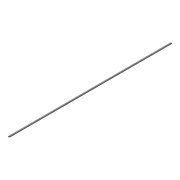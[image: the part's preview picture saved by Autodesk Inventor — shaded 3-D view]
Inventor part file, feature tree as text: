
AUTODESK INVENTOR PART (.ipt)
format: ipt  version: 2016 (Build 200138000, 138)  size: 67,584 bytes
history: native  units: in
note: dims shown in document units (in); Inventor stores cm internally (conversion verified against a paired STEP export)
features: extrude x1, sketch x1
ambient origin geometry x8: Origin, YZ Plane, XZ Plane, XY Plane, X Axis, Y Axis, Z Axis, Center Point
bodies: Solid1 (feature_tree)
feature tree (2):
  extrude  "Extrusion1"  Depth=472.4409in
  sketch  "Sketch1"  dims[d1=0.0906in d2=4.3307in d3=472.4409in d4=0.0in]
